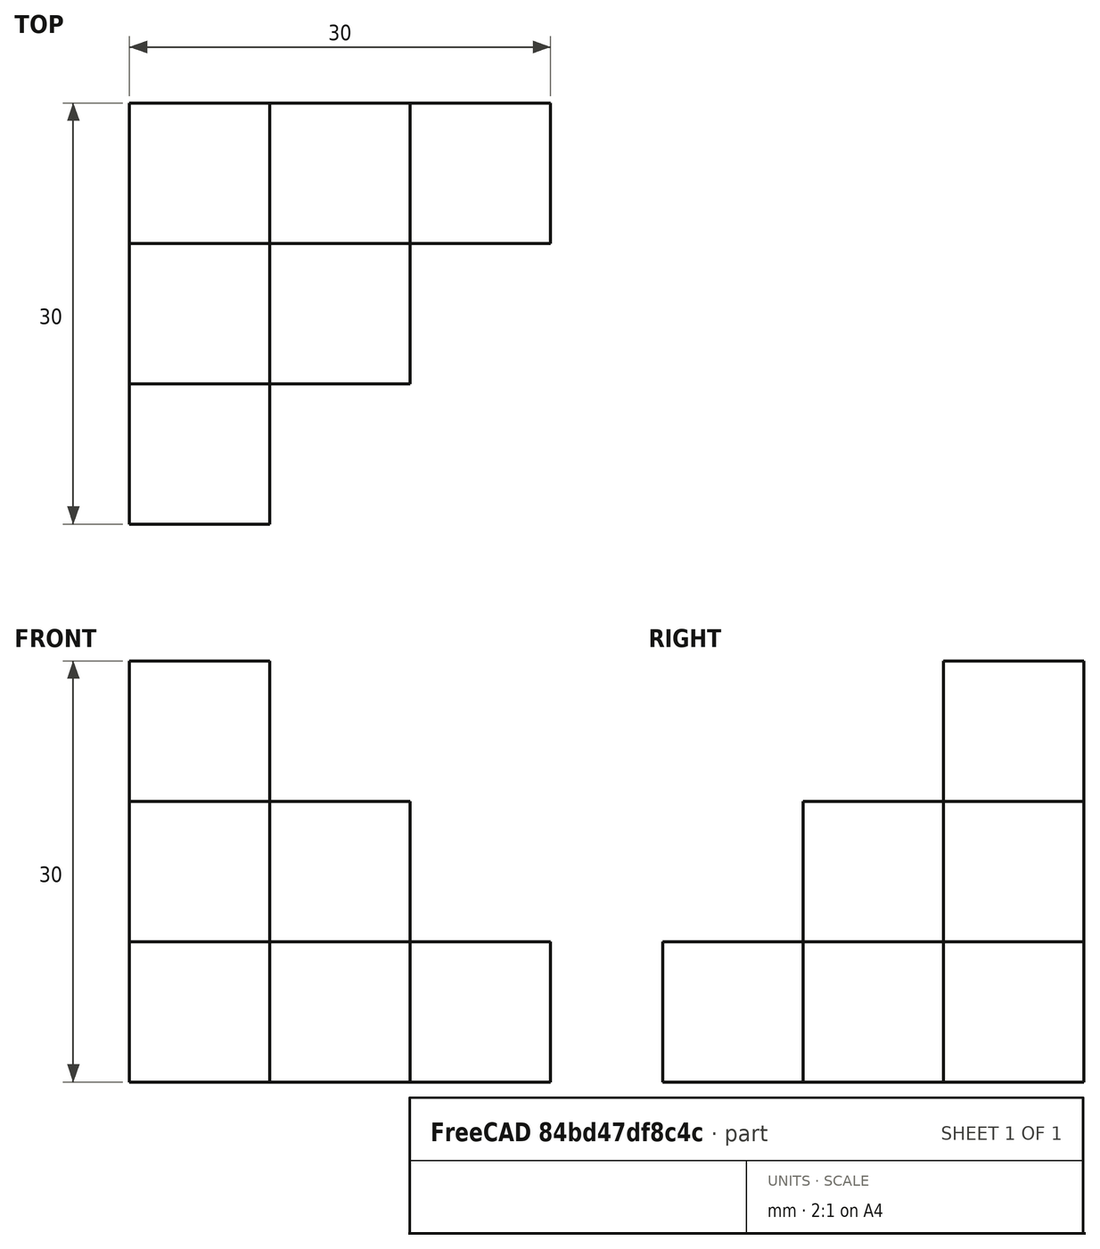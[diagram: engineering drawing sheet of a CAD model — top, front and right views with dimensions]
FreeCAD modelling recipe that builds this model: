
FCSTD DOCUMENT  (FreeCAD 0.21R33694 (Git))
Label: OJT1_T05R02_unions_qubert3
License: All rights reserved
LicenseURL: https://en.wikipedia.org/wiki/All_rights_reserved
objects: Part::Box×6, Part::MultiFuse×1, Part::Refine×1
note: 8 computed .brp shape members not serialized (recipe doc carries the construction recipe); baked Part::Feature solids carry a one-line shape summary decoded from their .brp

FEATURE [Part::Box] Box  label="Cub_de_dos_nivells1"
  AttacherType = Attacher::AttachEngine3D
  Height = 20
  Length = 10
  Placement = pos=(10,0,0) rot=(0,0,1;0rad)
  Width = 10
FEATURE [Part::Box] Box001  label="Cub_de_tres_nivells"
  AttacherType = Attacher::AttachEngine3D
  Height = 30
  Length = 10
  Width = 10
FEATURE [Part::Box] Box002  label="Cub_de_dos_nivells2"
  AttacherType = Attacher::AttachEngine3D
  Height = 20
  Length = 10
  Placement = pos=(0,-10,0) rot=(0,0,1;0rad)
  Width = 10
FEATURE [Part::Box] Box003  label="Cub_de_un_nivell1"
  AttacherType = Attacher::AttachEngine3D
  Height = 10
  Length = 10
  Placement = pos=(0,-20,0) rot=(0,0,1;0rad)
  Width = 10
FEATURE [Part::Box] Box004  label="Cub_de_un_nivell2"
  AttacherType = Attacher::AttachEngine3D
  Height = 10
  Length = 10
  Placement = pos=(10,-10,0) rot=(0,0,1;0rad)
  Width = 10
FEATURE [Part::Box] Box005  label="Cub_de_un_nivell3"
  AttacherType = Attacher::AttachEngine3D
  Height = 10
  Length = 10
  Placement = pos=(20,0,0) rot=(0,0,1;0rad)
  Width = 10
FEATURE [Part::MultiFuse] Fusion
  Shapes = -> [Box,Box001,Box002,Box003,Box004,Box005]
FEATURE [Part::Refine] Fusion001
  Source = -> Fusion
